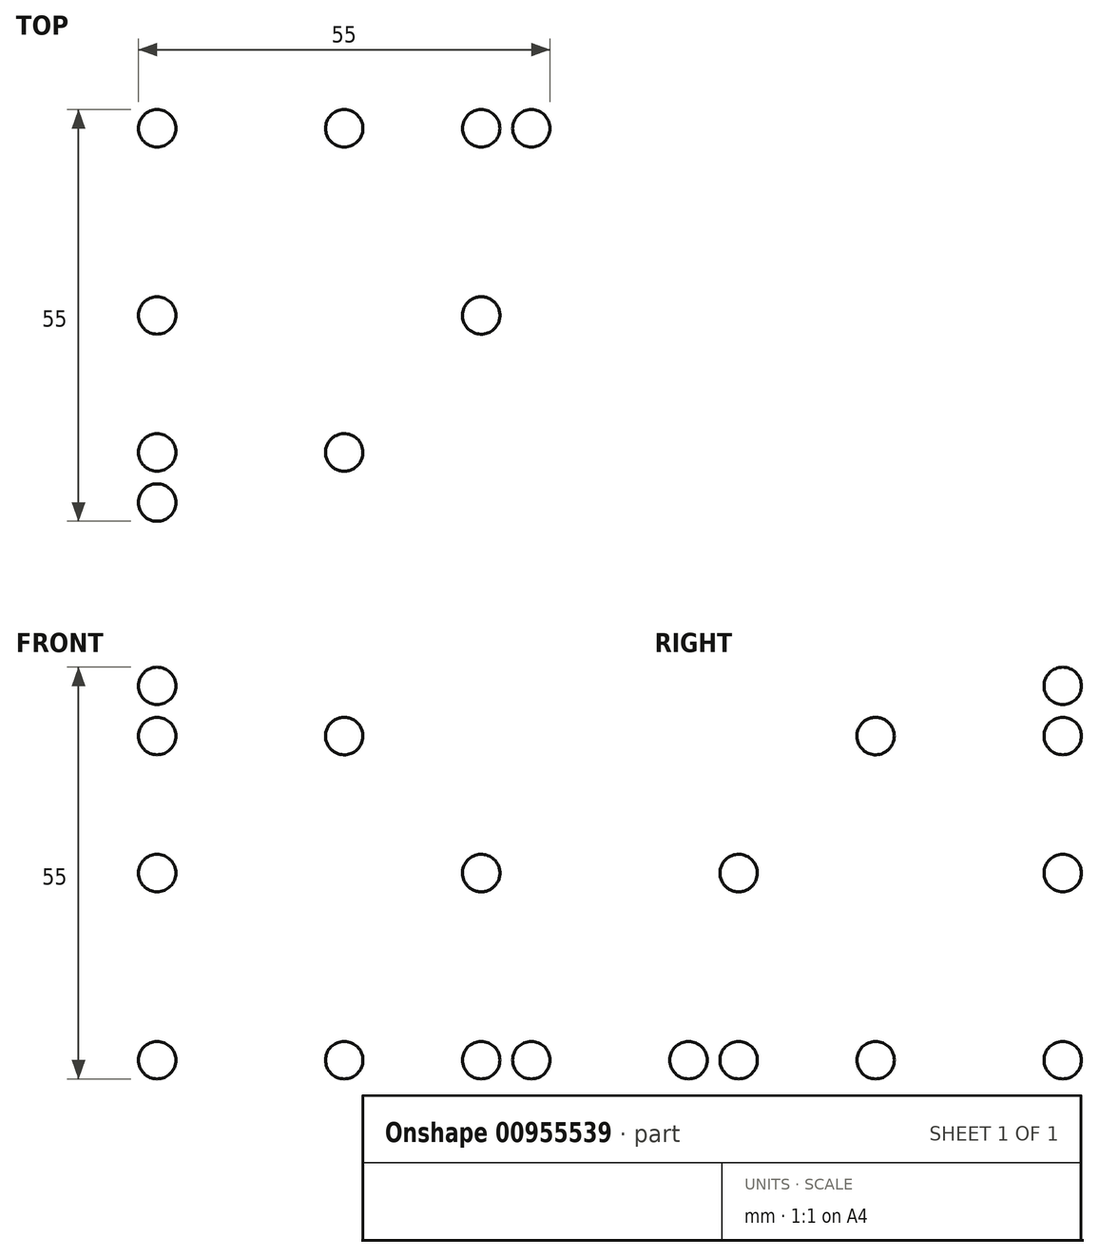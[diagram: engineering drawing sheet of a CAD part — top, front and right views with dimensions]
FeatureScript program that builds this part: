
annotation { "Feature Type Name" : "Feature", "Feature Type Description" : "" }
export const myFeature = defineFeature(function(context is Context, id is Id, definition is map)
    precondition{}
    {
        {
            var Q0;
            Q0=qCreatedBy(makeId("Front.planeOp"),FACE);
            var sketch = newSketch(context, id + "F0", { "sketchPlane" : qUnion([Q0])});
            skCircle(sketch, "E0", {"center": v(0, 0) * mm, "radius": 50 * mm});
            skLineSegment(sketch, "E1", {"start": v(0, 50) * mm, "end": v(0, -50) * mm});
            skLineSegment(sketch, "E2.1.0", {"start": v(25, 43.3) * mm, "end": v(-25, -43.3) * mm});
            skLineSegment(sketch, "E2.2.0", {"start": v(43.3, 25) * mm, "end": v(-43.3, -25) * mm});
            skLineSegment(sketch, "E2.3.0", {"start": v(50, 0) * mm, "end": v(-50, 0) * mm});
            skLineSegment(sketch, "E2.4.0", {"start": v(43.3, -25) * mm, "end": v(-43.3, 25) * mm});
            skLineSegment(sketch, "E2.5.0", {"start": v(25, -43.3) * mm, "end": v(-25, 43.3) * mm});
            skLineSegment(sketch, "E2.anchor1", {"start": v(0, 0) * mm, "end": v(0, -50) * mm, "construction": true});
            skLineSegment(sketch, "E2.anchor2", {"start": v(0, 0) * mm, "end": v(-25, 43.3) * mm, "construction": true});
            skSolve(sketch);
        }
        {
            var Q0;
            Q0=qCreatedBy(makeId("Right.planeOp"),FACE);
            var sketch = newSketch(context, id + "F1", { "sketchPlane" : qUnion([Q0])});
            skCircle(sketch, "E3", {"center": v(0, 0) * mm, "radius": 50 * mm});
            skLineSegment(sketch, "E4", {"start": v(0, 50) * mm, "end": v(0, -50) * mm});
            skLineSegment(sketch, "E5.1.0", {"start": v(25, 43.3) * mm, "end": v(-25, -43.3) * mm});
            skLineSegment(sketch, "E5.2.0", {"start": v(43.3, 25) * mm, "end": v(-43.3, -25) * mm});
            skLineSegment(sketch, "E5.3.0", {"start": v(50, 0) * mm, "end": v(-50, 0) * mm});
            skLineSegment(sketch, "E5.4.0", {"start": v(43.3, -25) * mm, "end": v(-43.3, 25) * mm});
            skLineSegment(sketch, "E5.5.0", {"start": v(25, -43.3) * mm, "end": v(-25, 43.3) * mm});
            skLineSegment(sketch, "E5.anchor1", {"start": v(0, 0) * mm, "end": v(0, -50) * mm, "construction": true});
            skLineSegment(sketch, "E5.anchor2", {"start": v(0, 0) * mm, "end": v(-25, 43.3) * mm, "construction": true});
            skSolve(sketch);
        }
        {
            var Q0;
            Q0=qCreatedBy(makeId("Top.planeOp"),FACE);
            var sketch = newSketch(context, id + "F2", { "sketchPlane" : qUnion([Q0])});
            skCircle(sketch, "E6", {"center": v(0, 0) * mm, "radius": 50 * mm});
            skLineSegment(sketch, "E7", {"start": v(0, 50) * mm, "end": v(0, -50) * mm});
            skLineSegment(sketch, "E8.1.0", {"start": v(25, 43.3) * mm, "end": v(-25, -43.3) * mm});
            skLineSegment(sketch, "E8.2.0", {"start": v(43.3, 25) * mm, "end": v(-43.3, -25) * mm});
            skLineSegment(sketch, "E8.3.0", {"start": v(50, 0) * mm, "end": v(-50, 0) * mm});
            skLineSegment(sketch, "E8.4.0", {"start": v(43.3, -25) * mm, "end": v(-43.3, 25) * mm});
            skLineSegment(sketch, "E8.5.0", {"start": v(25, -43.3) * mm, "end": v(-25, 43.3) * mm});
            skLineSegment(sketch, "E8.anchor1", {"start": v(0, 0) * mm, "end": v(0, -50) * mm, "construction": true});
            skLineSegment(sketch, "E8.anchor2", {"start": v(0, 0) * mm, "end": v(-25, 43.3) * mm, "construction": true});
            skSolve(sketch);
        }
        {
            var Q0;
            Q0=qCreatedBy(makeId("Right.planeOp"),FACE);
            var sketch = newSketch(context, id + "F3", { "sketchPlane" : qUnion([Q0])});
            skCircle(sketch, "E9", {"center": v(0, 50) * mm, "radius": 2.5 * mm});
            skLineSegment(sketch, "E10", {"start": v(0, 52.5) * mm, "end": v(0, 47.5) * mm});
            skSolve(sketch);
        }
        {
            var Q0;
            {var subQ0=sQuery(id+"F3.wireOp",EDGE,"E10");Q0=makeQuery(id+"F3.imprint","IMPRINT",FACE,{"disambiguationData":[TD([[makeQuery(id+"F3.imprint","IMPRINT",EDGE,{"derivedFrom":subQ0}),1.0]])]});}
            var Q1;
            Q1=sQuery(id+"F3.wireOp",EDGE,"E10");
            revolve(context, id + "F4", {"surfaceOperationType" : NewSurfaceOperationType.NEW, "entities" : qUnion([Q0]), "axis" : qUnion([Q1]), "revolveType" : RevolveType.FULL});
        }
        {
            var Q0;
            Q0=makeQuery(id+"F4.opRevolve","SWEPT_BODY",BODY,{"disambiguationData":[OSD([sQuery(id+"F3.wireOp",EDGE,"E9"),sQuery(id+"F3.wireOp",EDGE,"E10")])]});
            var Q1;
            Q1=sQuery(id+"F0.wireOp",EDGE,"E2.3.0");
            circularPattern(context, id + "F5", {"entities" : qUnion([Q0]), "axis" : qUnion([Q1]), "angle" : 90 * degree, "instanceCount" : 4, "oppositeDirection" : true, "equalSpace" : true});
        }
        {
            var Q0;
            Q0=makeQuery(id+"F5.opPattern","COPY",BODY,{"derivedFrom":makeQuery(id+"F4.opRevolve","SWEPT_BODY",BODY,{"disambiguationData":[OSD([sQuery(id+"F3.wireOp",EDGE,"E9"),sQuery(id+"F3.wireOp",EDGE,"E10")])]}),"instanceName":"1"});
            var Q1;
            Q1=makeQuery(id+"F5.opPattern","COPY",BODY,{"derivedFrom":makeQuery(id+"F4.opRevolve","SWEPT_BODY",BODY,{"disambiguationData":[OSD([sQuery(id+"F3.wireOp",EDGE,"E9"),sQuery(id+"F3.wireOp",EDGE,"E10")])]}),"instanceName":"2"});
            var Q2;
            Q2=makeQuery(id+"F5.opPattern","COPY",BODY,{"derivedFrom":makeQuery(id+"F4.opRevolve","SWEPT_BODY",BODY,{"disambiguationData":[OSD([sQuery(id+"F3.wireOp",EDGE,"E9"),sQuery(id+"F3.wireOp",EDGE,"E10")])]}),"instanceName":"3"});
            var Q3;
            Q3=sQuery(id+"F1.wireOp",EDGE,"E4");
            circularPattern(context, id + "F6", {"entities" : qUnion([Q0, Q1, Q2]), "axis" : qUnion([Q3]), "angle" : 90 * degree, "instanceCount" : 2, "oppositeDirection" : true, "equalSpace" : true});
        }
        {
            var Q0;
            Q0=makeQuery(id+"F5.opPattern","COPY",BODY,{"derivedFrom":makeQuery(id+"F4.opRevolve","SWEPT_BODY",BODY,{"disambiguationData":[OSD([sQuery(id+"F3.wireOp",EDGE,"E9"),sQuery(id+"F3.wireOp",EDGE,"E10")])]}),"instanceName":"2"});
            var Q1;
            Q1=makeQuery(id+"F5.opPattern","COPY",BODY,{"derivedFrom":makeQuery(id+"F4.opRevolve","SWEPT_BODY",BODY,{"disambiguationData":[OSD([sQuery(id+"F3.wireOp",EDGE,"E9"),sQuery(id+"F3.wireOp",EDGE,"E10")])]}),"instanceName":"1"});
            var Q2;
            Q2=sQuery(id+"F2.wireOp",EDGE,"E7");
            circularPattern(context, id + "F7", {"entities" : qUnion([Q0, Q1]), "axis" : qUnion([Q2]), "angle" : 90 * degree, "instanceCount" : 2, "oppositeDirection" : true, "equalSpace" : true});
        }
    });
